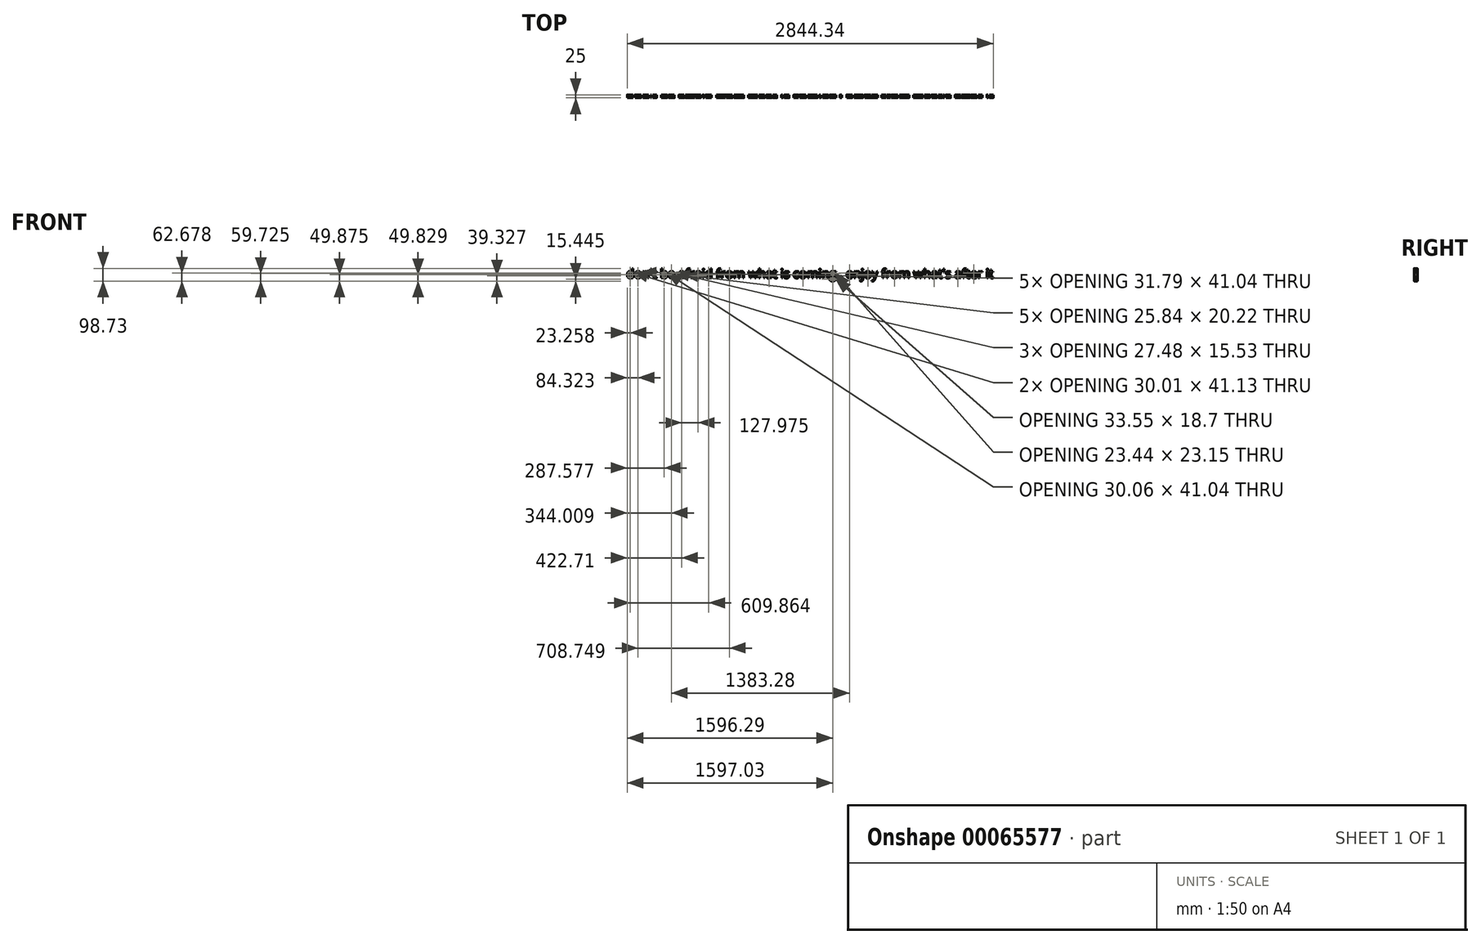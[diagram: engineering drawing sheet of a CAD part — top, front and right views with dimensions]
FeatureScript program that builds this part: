
annotation { "Feature Type Name" : "Feature", "Feature Type Description" : "" }
export const myFeature = defineFeature(function(context is Context, id is Id, definition is map)
    precondition{}
    {
        {
            var Q0;
            Q0=qCreatedBy(makeId("Front.planeOp"),FACE);
            var sketch = newSketch(context, id + "F0", { "sketchPlane" : qUnion([Q0])});
            skText(sketch, "E0", { "text": "don\'t be afraid from what is coming , enjoy from what\'s after it", "fontName": "OpenSans-Regular.ttf"});
            const initialGuessF0  = {"E0": [-0.08285, -0.03085, 1, 0, 0.0707]};
            skSetInitialGuess(sketch, initialGuessF0);
            skSolve(sketch);
        }
        {
            var Q0;
            Q0 = qSketchRegion(id + "F0", true);
            extrude(context, id + "F1", {"entities" : qUnion([Q0]), "depth" : 25 * mm});
        }
    });
